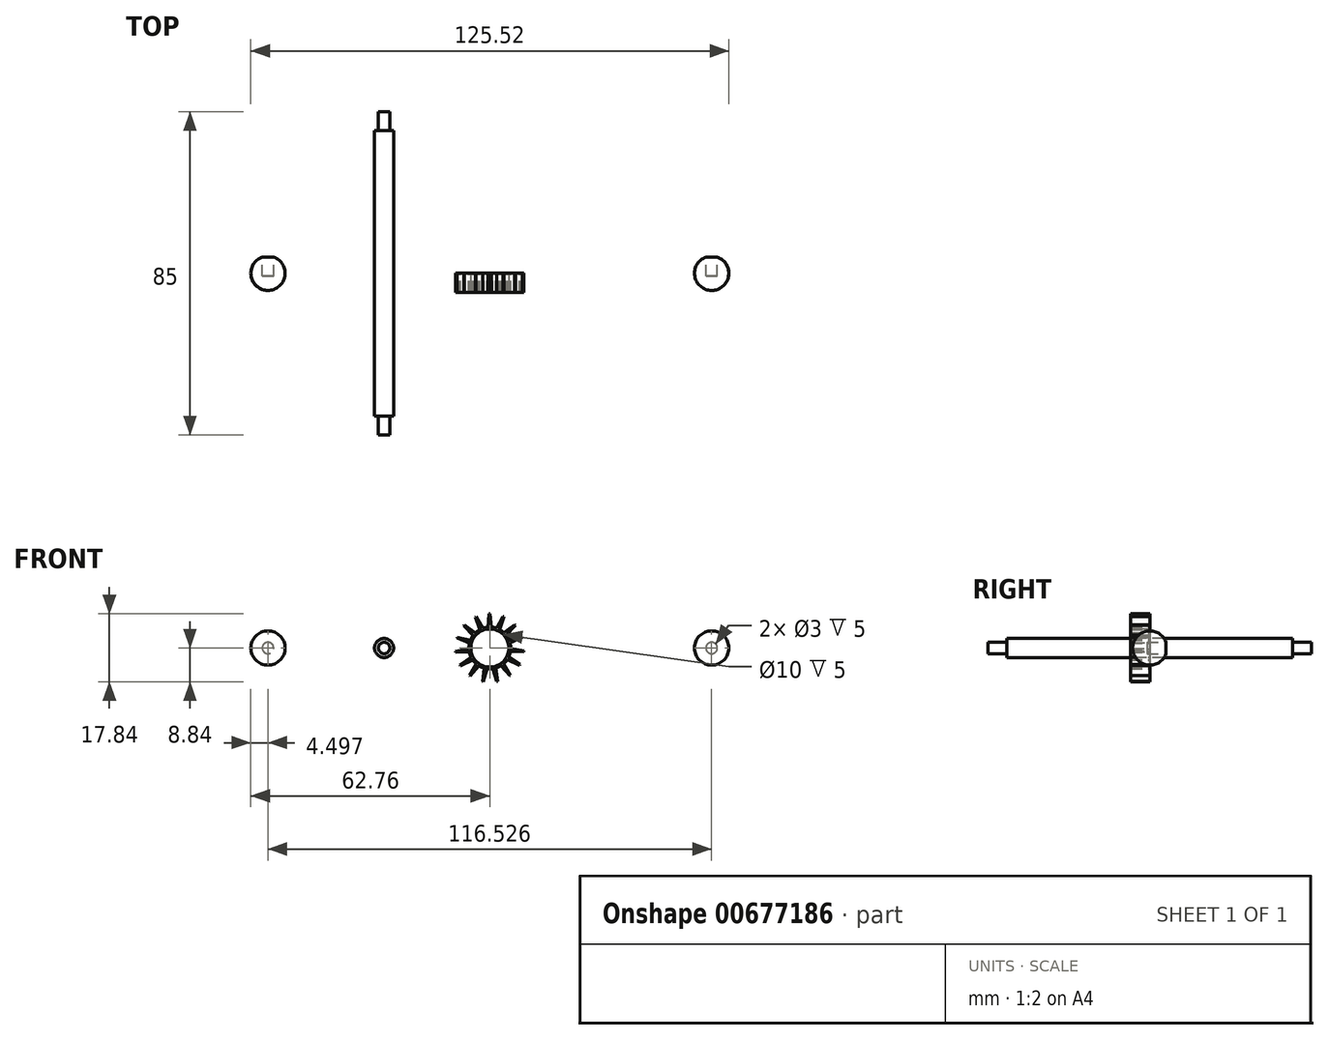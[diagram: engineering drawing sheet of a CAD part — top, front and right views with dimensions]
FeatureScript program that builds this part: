
annotation { "Feature Type Name" : "Feature", "Feature Type Description" : "" }
export const myFeature = defineFeature(function(context is Context, id is Id, definition is map)
    precondition{}
    {
        {
            var Q0;
            Q0=qCreatedBy(makeId("Front.planeOp"),FACE);
            var sketch = newSketch(context, id + "F0", { "sketchPlane" : qUnion([Q0])});
            skCircle(sketch, "E0", {"center": v(0, 0) * mm, "radius": 5.5 * mm});
            skLineSegment(sketch, "E1", {"start": v(-0.45, 5.48) * mm, "end": v(-0.17, 9) * mm});
            skLineSegment(sketch, "E2", {"start": v(-0.17, 9) * mm, "end": v(0.03, 9) * mm});
            skLineSegment(sketch, "E3", {"start": v(0.03, 9) * mm, "end": v(0.37, 5.49) * mm});
            skSolve(sketch);
        }
        {
            var Q0;
            Q0 = qSketchRegion(id + "F0", true);
            extrude(context, id + "F1", {"entities" : qUnion([Q0]), "depth" : 5 * mm, "offsetDistance" : 25 * mm});
        }
        {
            var Q0;
            Q0=makeQuery(id+"F1.opExtrude","SWEPT_FACE",FACE,{"disambiguationData":[OSD([sQuery(id+"F0.wireOp",EDGE,"E3")])]});
            var Q1;
            Q1=makeQuery(id+"F1.opExtrude","SWEPT_FACE",FACE,{"disambiguationData":[OSD([sQuery(id+"F0.wireOp",EDGE,"E1")])]});
            var Q2;
            Q2=makeQuery(id+"F1.opExtrude","SWEPT_FACE",FACE,{"disambiguationData":[OSD([sQuery(id+"F0.wireOp",EDGE,"E2")])]});
            var Q3;
            Q3=makeQuery(id+"F1.opExtrude","SWEPT_FACE",FACE,{"disambiguationData":[OSD([sQuery(id+"F0.wireOp",EDGE,"E0")])]});
            circularPattern(context, id + "F2", {"patternType" : PatternType.FACE, "faces" : qUnion([Q0, Q1, Q2]), "axis" : qUnion([Q3]), "angle" : 360 * degree, "instanceCount" : 15, "equalSpace" : true});
        }
        {
            var Q0;
            Q0=makeQuery(id+"F1.opExtrude","CAP_FACE",FACE,{"disambiguationData":[OSD([sQuery(id+"F0.wireOp",EDGE,"E0"),sQuery(id+"F0.wireOp",EDGE,"E1"),sQuery(id+"F0.wireOp",EDGE,"E2"),sQuery(id+"F0.wireOp",EDGE,"E3")])],"isStart":false});
            var sketch = newSketch(context, id + "F3", { "sketchPlane" : qUnion([Q0])});
            skCircle(sketch, "E4", {"center": v(0, 0) * mm, "radius": 5 * mm});
            skSolve(sketch);
        }
        {
            var Q0;
            Q0 = qSketchRegion(id + "F3", true);
            extrude(context, id + "F4", {"entities" : qUnion([Q0]), "operationType" : NewBodyOperationType.REMOVE, "oppositeDirection" : true, "depth" : 25 * mm, "offsetDistance" : 25 * mm});
        }
        {
            var Q0;
            Q0=qCreatedBy(makeId("Front.planeOp"),FACE);
            var sketch = newSketch(context, id + "F5", { "sketchPlane" : qUnion([Q0])});
            skCircle(sketch, "E5", {"center": v(-27.77, 0) * mm, "radius": 2.5 * mm});
            skSolve(sketch);
        }
        {
            var Q0;
            Q0 = qSketchRegion(id + "F5", true);
            extrude(context, id + "F6", {"entities" : qUnion([Q0]), "endBound" : BoundingType.SYMMETRIC, "depth" : 75 * mm, "offsetDistance" : 25 * mm});
        }
        {
            var Q0;
            Q0=makeQuery(id+"F6.opExtrude","CAP_FACE",FACE,{"disambiguationData":[OSD([sQuery(id+"F5.wireOp",EDGE,"E5")])],"isStart":false});
            var sketch = newSketch(context, id + "F7", { "sketchPlane" : qUnion([Q0])});
            skCircle(sketch, "E6", {"center": v(-27.77, 0) * mm, "radius": 1.5 * mm});
            skSolve(sketch);
        }
        {
            var Q0;
            Q0 = qSketchRegion(id + "F7", true);
            extrude(context, id + "F8", {"entities" : qUnion([Q0]), "operationType" : NewBodyOperationType.ADD, "depth" : 5 * mm, "offsetDistance" : 25 * mm});
        }
        {
            var Q0;
            Q0=makeQuery(id+"F6.opExtrude","SWEPT_BODY",BODY,{"disambiguationData":[OSD([sQuery(id+"F5.wireOp",EDGE,"E5")])]});
            var Q1;
            Q1=qCreatedBy(makeId("Front.planeOp"),FACE);
            mirror(context, id + "F9", {"operationType" : NewBodyOperationType.ADD, "entities" : qUnion([Q0]), "mirrorPlane" : qUnion([Q1])});
        }
        {
            var Q0;
            Q0=qCreatedBy(makeId("Top.planeOp"),FACE);
            var sketch = newSketch(context, id + "F10", { "sketchPlane" : qUnion([Q0])});
            skArc(sketch, "E7", {"start": v(-58.26, -4.5) * mm, "mid": v(-53.83, -0.76) * mm, "end": v(-56.76, 4.24) * mm});
            skLineSegment(sketch, "E8", {"start": v(-58.26, 0) * mm, "end": v(-58.26, 4.24) * mm});
            skLineSegment(sketch, "E9", {"start": v(-58.26, 0) * mm, "end": v(-58.26, -4.5) * mm});
            skLineSegment(sketch, "E10", {"start": v(-58.26, 4.24) * mm, "end": v(-56.76, 4.24) * mm});
            skSolve(sketch);
        }
        {
            var Q0;
            Q0 = qSketchRegion(id + "F10", true);
            var Q1;
            Q1=sQuery(id+"F10.wireOp",EDGE,"E9");
            revolve(context, id + "F11", {"entities" : qUnion([Q0]), "axis" : qUnion([Q1]), "revolveType" : RevolveType.FULL});
        }
        {
            var Q0;
            Q0=makeQuery(id+"F11.opRevolve","SWEPT_FACE",FACE,{"disambiguationData":[OSD([sQuery(id+"F10.wireOp",EDGE,"E10")])]});
            extrude(context, id + "F12", {"entities" : qUnion([Q0]), "operationType" : NewBodyOperationType.REMOVE, "oppositeDirection" : true, "depth" : 5 * mm, "offsetDistance" : 25 * mm});
        }
        {
            var Q0;
            Q0=makeQuery(id+"F11.opRevolve","SWEPT_BODY",BODY,{"disambiguationData":[OSD([sQuery(id+"F10.wireOp",EDGE,"E7"),sQuery(id+"F10.wireOp",EDGE,"E8"),sQuery(id+"F10.wireOp",EDGE,"E9"),sQuery(id+"F10.wireOp",EDGE,"E10")])]});
            var Q1;
            Q1=qCreatedBy(makeId("Right.planeOp"),FACE);
            mirror(context, id + "F13", {"entities" : qUnion([Q0]), "mirrorPlane" : qUnion([Q1])});
        }
    });
